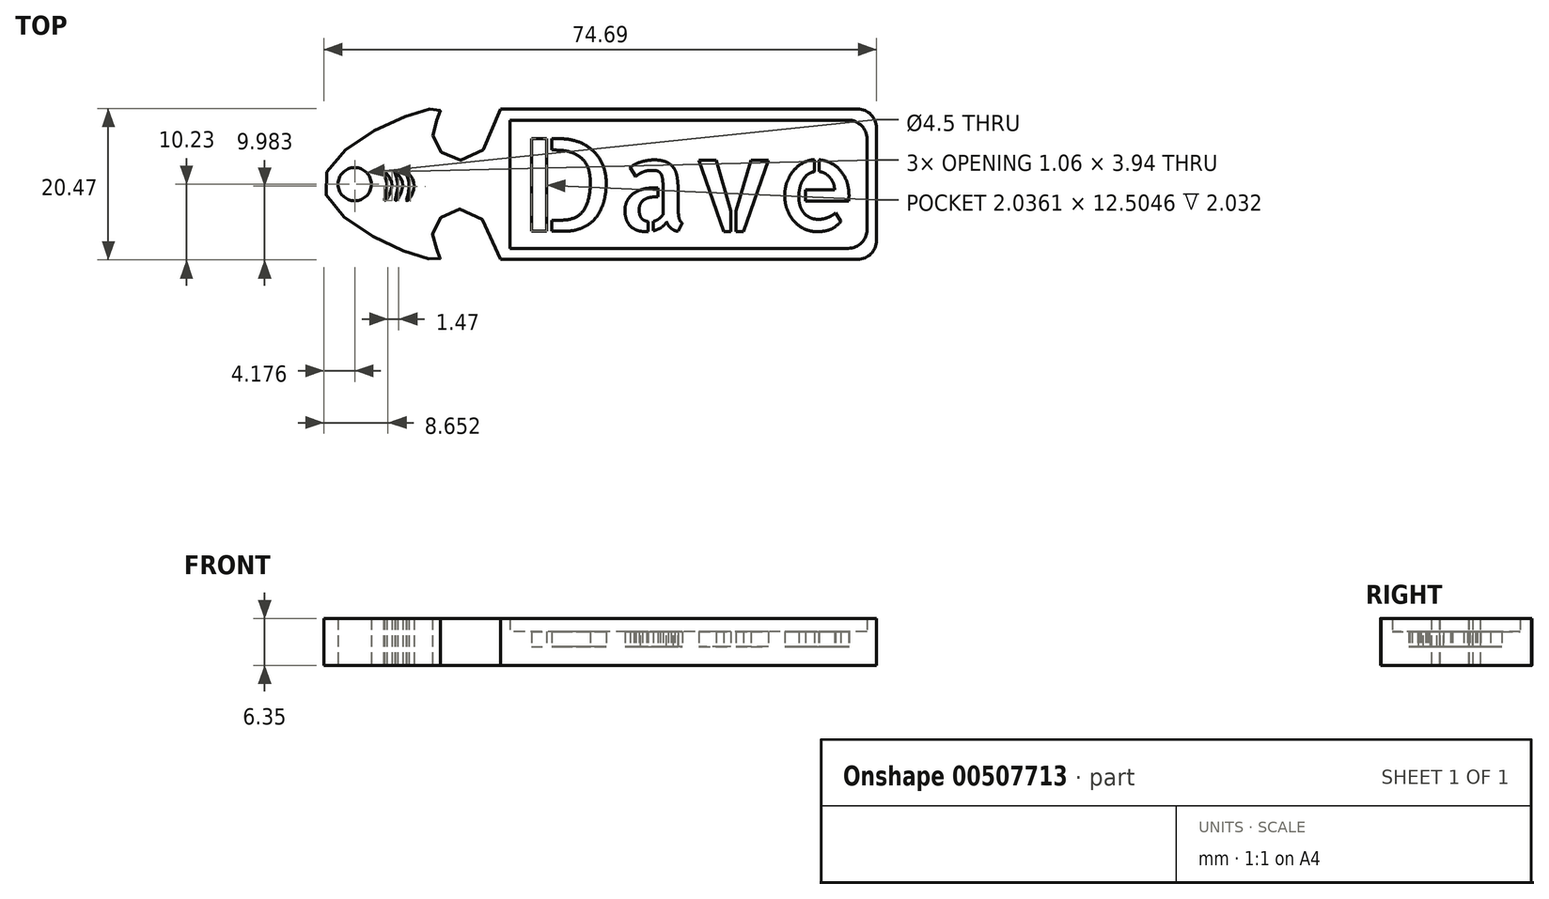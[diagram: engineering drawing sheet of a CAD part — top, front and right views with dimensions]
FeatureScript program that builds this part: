
annotation { "Feature Type Name" : "Feature", "Feature Type Description" : "" }
export const myFeature = defineFeature(function(context is Context, id is Id, definition is map)
    precondition{}
    {
        {
            var Q0;
            Q0=qCreatedBy(makeId("Top.planeOp"),FACE);
            var sketch = newSketch(context, id + "F0", { "sketchPlane" : qUnion([Q0])});
            skLineSegment(sketch, "E0.bottom", {"start": v(22.86, 10.16) * mm, "end": v(-25.4, 10.16) * mm});
            skLineSegment(sketch, "E0.top", {"start": v(25.4, -10.16) * mm, "end": v(-25.4, -10.16) * mm});
            skLineSegment(sketch, "E0.left", {"start": v(25.4, 7.62) * mm, "end": v(25.4, -10.16) * mm});
            skLineSegment(sketch, "E0.right", {"start": v(-25.4, 10.16) * mm, "end": v(-25.4, -10.16) * mm});
            skPoint(sketch, "E0.middle", {"position": v(0, 0) * mm});
            skText(sketch, "E1", { "text": "Dave", "fontName": "AllertaStencil-Regular.ttf"});
            skFitSpline(sketch, "E2", {"points": [v(-25.4, 10.16) * mm, v(-34.53, 6.16) * mm, v(-33.7, 10.16) * mm, v(-49.29, 0) * mm, v(-33.7, -10.16) * mm, v(-34.56, -6.35) * mm, v(-25.4, -10.16) * mm], "startDerivative": vector(-38.56, -183.9) * mm, "endDerivative": vector(41.99, -183.17) * mm});
            skCircle(sketch, "E3", {"center": v(-45.11, 0) * mm, "radius": 2.25 * mm});
            skFitSpline(sketch, "E4", {"points": [v(-41.17, 1.72) * mm, v(-40.1, 0) * mm, v(-41.07, -2.22) * mm, v(-40.78, 0) * mm, v(-41.17, 1.72) * mm]});
            skFitSpline(sketch, "E5", {"points": [v(-39.7, 1.72) * mm, v(-38.64, 0) * mm, v(-39.6, -2.22) * mm, v(-39.31, 0) * mm, v(-39.7, 1.72) * mm]});
            skFitSpline(sketch, "E6", {"points": [v(-38.15, 1.66) * mm, v(-37.09, -0.06) * mm, v(-38.05, -2.29) * mm, v(-37.76, -0.06) * mm, v(-38.15, 1.66) * mm]});
            skLineSegment(sketch, "E7.bottom", {"start": v(21.59, 8.66) * mm, "end": v(-24.13, 8.66) * mm});
            skLineSegment(sketch, "E7.top", {"start": v(21.6, -8.66) * mm, "end": v(-24.13, -8.66) * mm});
            skLineSegment(sketch, "E7.left", {"start": v(24.13, 6.12) * mm, "end": v(24.13, -6.12) * mm});
            skLineSegment(sketch, "E7.right", {"start": v(-24.13, 8.66) * mm, "end": v(-24.13, -8.66) * mm});
            skPoint(sketch, "E8.visualSharp", {"position": v(25.4, 10.16) * mm});
            skArc(sketch, "E8.filletArc", {"start": v(25.4, 7.62) * mm, "mid": v(24.66, 9.42) * mm, "end": v(22.86, 10.16) * mm});
            skPoint(sketch, "E9.visualSharp", {"position": v(24.13, 8.66) * mm});
            skArc(sketch, "E9.filletArc", {"start": v(24.13, 6.12) * mm, "mid": v(23.39, 7.92) * mm, "end": v(21.59, 8.66) * mm});
            skPoint(sketch, "E10.visualSharp", {"position": v(24.13, -8.66) * mm});
            skArc(sketch, "E10.filletArc", {"start": v(21.6, -8.66) * mm, "mid": v(23.39, -7.92) * mm, "end": v(24.13, -6.12) * mm});
            const initialGuessF0  = {"E1": [-0.02286, -0.00635, 1, 0, 0.01251]};
            skSetInitialGuess(sketch, initialGuessF0);
            skSolve(sketch);
        }
        {
            var Q0;
            Q0=makeQuery(id+"F0.imprint","IMPRINT",FACE,{"disambiguationData":[TD([[makeQuery(id+"F0.imprint","IMPRINT",EDGE,{"derivedFrom":sQuery(id+"F0.wireOp",EDGE,"E1.sketch_text.stroke-0")}),-1.0]])]});
            var Q1;
            Q1=makeQuery(id+"F0.imprint","IMPRINT",FACE,{"disambiguationData":[TD([[makeQuery(id+"F0.imprint","IMPRINT",EDGE,{"derivedFrom":sQuery(id+"F0.wireOp",EDGE,"E1.sketch_text.stroke-4")}),-1.0]])]});
            var Q2;
            Q2=makeQuery(id+"F0.imprint","IMPRINT",FACE,{"disambiguationData":[TD([[makeQuery(id+"F0.imprint","IMPRINT",EDGE,{"derivedFrom":sQuery(id+"F0.wireOp",EDGE,"E1.sketch_text.stroke-45")}),-1.0]])]});
            var Q3;
            Q3=makeQuery(id+"F0.imprint","IMPRINT",FACE,{"disambiguationData":[TD([[makeQuery(id+"F0.imprint","IMPRINT",EDGE,{"derivedFrom":sQuery(id+"F0.wireOp",EDGE,"E1.sketch_text.stroke-26")}),-1.0]])]});
            var Q4;
            Q4=makeQuery(id+"F0.imprint","IMPRINT",FACE,{"disambiguationData":[TD([[makeQuery(id+"F0.imprint","IMPRINT",EDGE,{"derivedFrom":sQuery(id+"F0.wireOp",EDGE,"E1.sketch_text.stroke-81")}),-1.0]])]});
            var Q5;
            Q5=makeQuery(id+"F0.imprint","IMPRINT",FACE,{"disambiguationData":[TD([[makeQuery(id+"F0.imprint","IMPRINT",EDGE,{"derivedFrom":sQuery(id+"F0.wireOp",EDGE,"E1.sketch_text.stroke-86")}),-1.0]])]});
            var Q6;
            Q6=makeQuery(id+"F0.imprint","IMPRINT",FACE,{"disambiguationData":[TD([[makeQuery(id+"F0.imprint","IMPRINT",EDGE,{"derivedFrom":sQuery(id+"F0.wireOp",EDGE,"E1.sketch_text.stroke-104")}),-1.0]])]});
            var Q7;
            Q7=makeQuery(id+"F0.imprint","IMPRINT",FACE,{"disambiguationData":[TD([[makeQuery(id+"F0.imprint","IMPRINT",EDGE,{"derivedFrom":sQuery(id+"F0.wireOp",EDGE,"E1.sketch_text.stroke-91")}),-1.0]])]});
            extrude(context, id + "F1", {"entities" : qUnion([Q0, Q1, Q2, Q3, Q4, Q5, Q6, Q7]), "depth" : 2.54 * mm});
        }
        {
            var Q0;
            Q0=makeQuery(id+"F0.imprint","IMPRINT",FACE,{"disambiguationData":[TD([[makeQuery(id+"F0.imprint","IMPRINT",EDGE,{"derivedFrom":sQuery(id+"F0.wireOp",EDGE,"E0.bottom")}),1.0]])]});
            var Q1;
            Q1=makeQuery(id+"F0.imprint","IMPRINT",FACE,{"disambiguationData":[TD([[makeQuery(id+"F0.imprint","IMPRINT",EDGE,{"derivedFrom":sQuery(id+"F0.wireOp",EDGE,"E0.right")}),-1.0]])]});
            extrude(context, id + "F2", {"entities" : qUnion([Q0, Q1]), "operationType" : NewBodyOperationType.ADD, "depth" : 6.35 * mm});
        }
        {
            var Q0;
            Q0=makeQuery(id+"F0.imprint","IMPRINT",FACE,{"disambiguationData":[TD([[makeQuery(id+"F0.imprint","IMPRINT",EDGE,{"derivedFrom":sQuery(id+"F0.wireOp",EDGE,"E1.sketch_text.stroke-0")}),1.0]])]});
            extrude(context, id + "F3", {"entities" : qUnion([Q0]), "operationType" : NewBodyOperationType.ADD, "depth" : 4.57 * mm});
        }
        {
            var Q0;
            Q0=makeQuery(id+"F2.opExtrude","SWEPT_EDGE",EDGE,{"disambiguationData":[OSD([sQuery(id+"F0.wireOp",EDGE,"E0.left"),sQuery(id+"F0.wireOp",EDGE,"E0.top")])]});
            fillet(context, id + "F4", {"entities" : qUnion([Q0]), "radius" : 2.54 * mm, "tangentPropagation" : true, "allowEdgeOverflow" : false});
        }
    });
